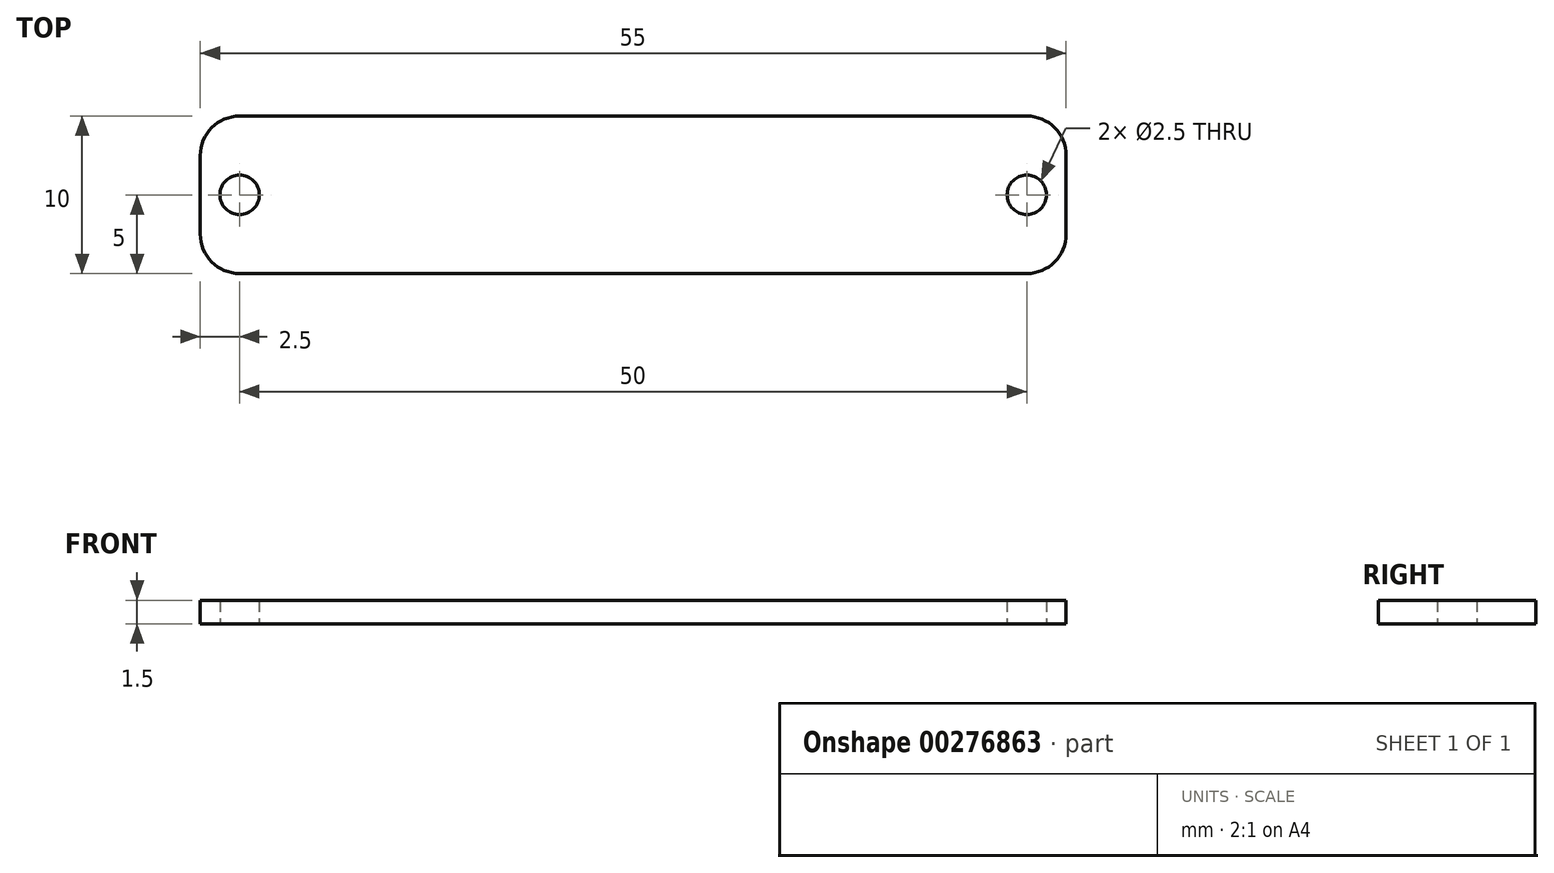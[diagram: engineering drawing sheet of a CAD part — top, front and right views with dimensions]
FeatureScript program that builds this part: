
annotation { "Feature Type Name" : "Feature", "Feature Type Description" : "" }
export const myFeature = defineFeature(function(context is Context, id is Id, definition is map)
    precondition{}
    {
        {
            var Q0;
            Q0=qCreatedBy(makeId("Top.planeOp"),FACE);
            var sketch = newSketch(context, id + "F0", { "sketchPlane" : qUnion([Q0])});
            skLineSegment(sketch, "E0.bottom", {"start": v(25, 5) * mm, "end": v(-25, 5) * mm});
            skLineSegment(sketch, "E0.top", {"start": v(25, -5) * mm, "end": v(-25, -5) * mm});
            skLineSegment(sketch, "E0.left", {"start": v(27.5, 2.5) * mm, "end": v(27.5, -2.5) * mm});
            skLineSegment(sketch, "E0.right", {"start": v(-27.5, 2.5) * mm, "end": v(-27.5, -2.5) * mm});
            skPoint(sketch, "E0.middle", {"position": v(0, 0) * mm});
            skPoint(sketch, "E1.visualSharp", {"position": v(-27.5, 5) * mm});
            skArc(sketch, "E1.filletArc", {"start": v(-25, 5) * mm, "mid": v(-26.77, 4.27) * mm, "end": v(-27.5, 2.5) * mm});
            skPoint(sketch, "E2.visualSharp", {"position": v(-27.5, -5) * mm});
            skArc(sketch, "E2.filletArc", {"start": v(-27.5, -2.5) * mm, "mid": v(-26.77, -4.27) * mm, "end": v(-25, -5) * mm});
            skPoint(sketch, "E3.visualSharp", {"position": v(27.5, 5) * mm});
            skArc(sketch, "E3.filletArc", {"start": v(27.5, 2.5) * mm, "mid": v(26.77, 4.27) * mm, "end": v(25, 5) * mm});
            skPoint(sketch, "E4.visualSharp", {"position": v(27.5, -5) * mm});
            skArc(sketch, "E4.filletArc", {"start": v(25, -5) * mm, "mid": v(26.77, -4.27) * mm, "end": v(27.5, -2.5) * mm});
            skLineSegment(sketch, "E5", {"start": v(0, 0) * mm, "end": v(-25, 0) * mm});
            skLineSegment(sketch, "E6", {"start": v(0, 0) * mm, "end": v(25, 0) * mm});
            skCircle(sketch, "E7", {"center": v(-25, 0) * mm, "radius": 1.25 * mm});
            skCircle(sketch, "E8", {"center": v(25, 0) * mm, "radius": 1.25 * mm});
            skSolve(sketch);
        }
        {
            var Q0;
            Q0 = qSketchRegion(id + "F0", true);
            extrude(context, id + "F1", {"entities" : qUnion([Q0]), "depth" : 1.5 * mm});
        }
    });
